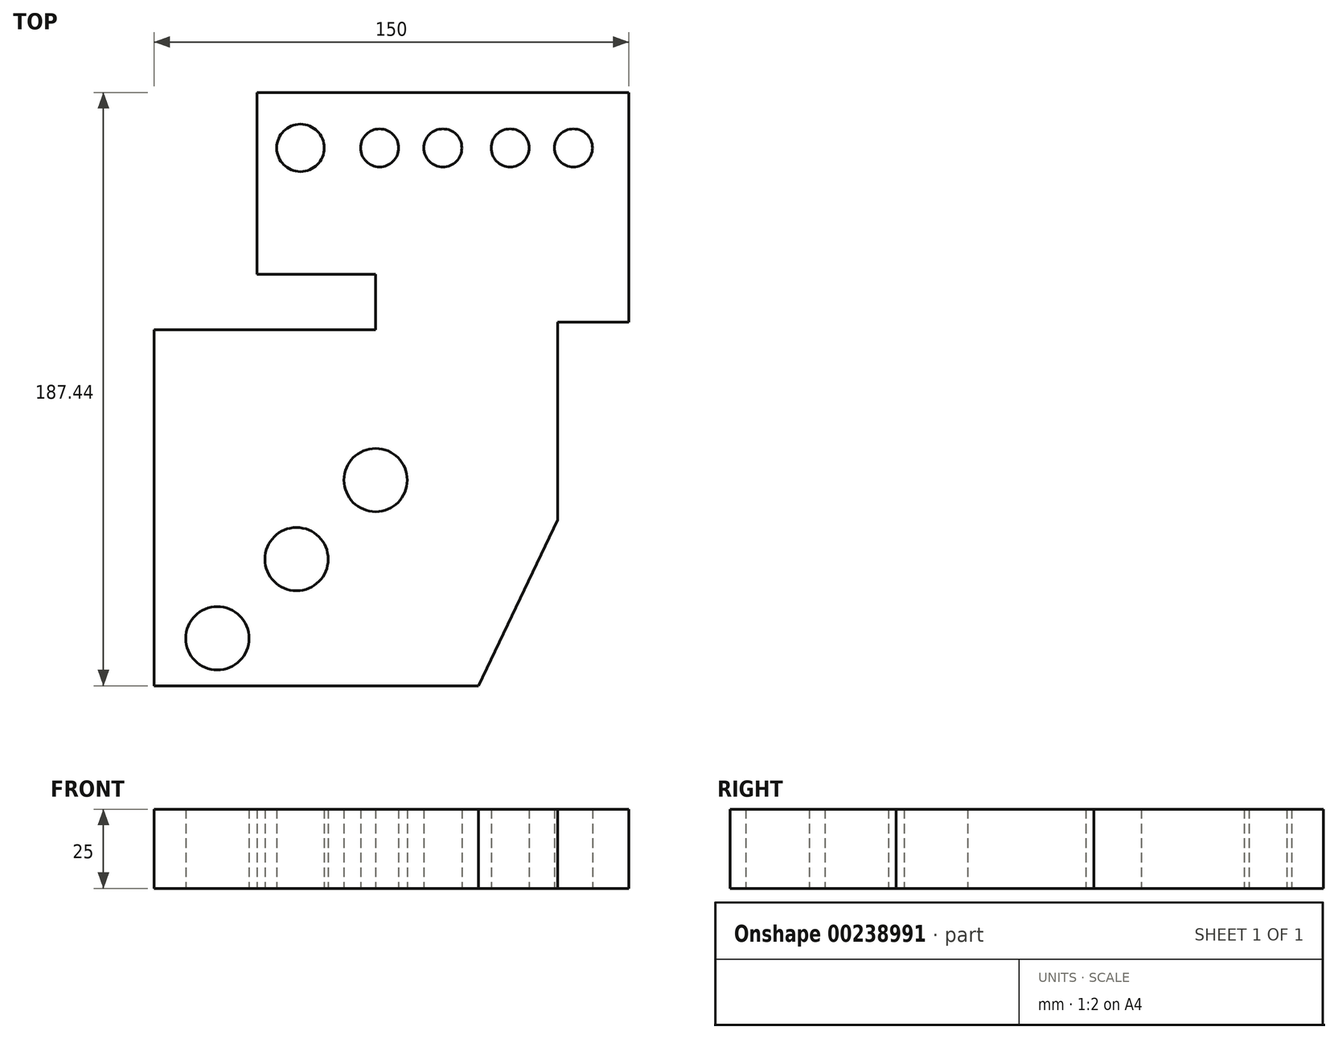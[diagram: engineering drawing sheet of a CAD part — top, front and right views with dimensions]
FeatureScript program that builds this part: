
annotation { "Feature Type Name" : "Feature", "Feature Type Description" : "" }
export const myFeature = defineFeature(function(context is Context, id is Id, definition is map)
    precondition{}
    {
        {
            var Q0;
            Q0=qCreatedBy(makeId("Top.planeOp"),FACE);
            var sketch = newSketch(context, id + "F0", { "sketchPlane" : qUnion([Q0])});
            skLineSegment(sketch, "E0", {"start": v(-120.25, -66.32) * mm, "end": v(-17.75, -66.32) * mm});
            skLineSegment(sketch, "E1", {"start": v(-120.25, -66.32) * mm, "end": v(-120.25, 46.12) * mm});
            skLineSegment(sketch, "E2", {"start": v(-120.25, 46.12) * mm, "end": v(-50.25, 46.12) * mm});
            skLineSegment(sketch, "E3", {"start": v(-50.25, 46.12) * mm, "end": v(-50.25, 63.62) * mm});
            skLineSegment(sketch, "E4", {"start": v(-50.25, 63.62) * mm, "end": v(-87.75, 63.62) * mm});
            skLineSegment(sketch, "E5", {"start": v(-87.75, 63.62) * mm, "end": v(-87.75, 121.12) * mm});
            skLineSegment(sketch, "E6", {"start": v(-87.75, 121.12) * mm, "end": v(29.75, 121.12) * mm});
            skLineSegment(sketch, "E7", {"start": v(29.75, 121.12) * mm, "end": v(29.75, 48.62) * mm});
            skLineSegment(sketch, "E8", {"start": v(29.75, 48.62) * mm, "end": v(7.25, 48.62) * mm});
            skLineSegment(sketch, "E9", {"start": v(7.25, 48.62) * mm, "end": v(7.25, -13.88) * mm});
            skLineSegment(sketch, "E10", {"start": v(7.25, -13.88) * mm, "end": v(-17.75, -66.32) * mm});
            skLineSegment(sketch, "E11", {"start": v(-120.25, -66.32) * mm, "end": v(-100.25, -66.32) * mm});
            skLineSegment(sketch, "E12", {"start": v(-120.25, -66.32) * mm, "end": v(-120.25, -51.32) * mm});
            skLineSegment(sketch, "E13", {"start": v(-120.25, -51.32) * mm, "end": v(-100.25, -51.32) * mm});
            skCircle(sketch, "E14", {"center": v(-100.25, -51.32) * mm, "radius": 10 * mm});
            skLineSegment(sketch, "E15", {"start": v(-100.25, -66.32) * mm, "end": v(-75.25, -66.32) * mm});
            skLineSegment(sketch, "E16", {"start": v(-120.25, -51.32) * mm, "end": v(-120.25, -26.32) * mm});
            skLineSegment(sketch, "E17", {"start": v(-120.25, -26.32) * mm, "end": v(-75.25, -26.32) * mm});
            skCircle(sketch, "E18", {"center": v(-75.25, -26.32) * mm, "radius": 10 * mm});
            skLineSegment(sketch, "E19", {"start": v(-120.25, -26.32) * mm, "end": v(-120.25, -1.32) * mm});
            skLineSegment(sketch, "E20", {"start": v(-75.25, -66.32) * mm, "end": v(-50.25, -66.32) * mm});
            skLineSegment(sketch, "E21", {"start": v(-120.25, -1.32) * mm, "end": v(-50.25, -1.32) * mm});
            skCircle(sketch, "E22", {"center": v(-50.25, -1.32) * mm, "radius": 10 * mm});
            skLineSegment(sketch, "E23", {"start": v(29.75, 121.12) * mm, "end": v(29.75, 103.62) * mm});
            skLineSegment(sketch, "E24", {"start": v(29.75, 121.12) * mm, "end": v(12.25, 121.12) * mm});
            skLineSegment(sketch, "E25", {"start": v(12.25, 121.12) * mm, "end": v(12.25, 103.62) * mm});
            skCircle(sketch, "E26", {"center": v(12.25, 103.62) * mm, "radius": 6 * mm});
            skLineSegment(sketch, "E27", {"start": v(12.25, 121.12) * mm, "end": v(-7.75, 121.12) * mm});
            skLineSegment(sketch, "E28", {"start": v(-7.75, 121.12) * mm, "end": v(-7.75, 103.62) * mm});
            skCircle(sketch, "E29", {"center": v(-7.75, 103.62) * mm, "radius": 6 * mm});
            skLineSegment(sketch, "E30", {"start": v(-103.8, 126.74) * mm, "end": v(-82.76, 132.44) * mm, "construction": true});
            skLineSegment(sketch, "E31", {"start": v(-7.75, 121.12) * mm, "end": v(-29, 121.12) * mm, "construction": true});
            skLineSegment(sketch, "E32", {"start": v(-29, 121.12) * mm, "end": v(-29, 103.62) * mm});
            skCircle(sketch, "E33", {"center": v(-29, 103.62) * mm, "radius": 6 * mm});
            skLineSegment(sketch, "E34", {"start": v(-29, 121.12) * mm, "end": v(-49, 121.12) * mm});
            skLineSegment(sketch, "E35", {"start": v(-49, 121.12) * mm, "end": v(-49, 103.62) * mm});
            skCircle(sketch, "E36", {"center": v(-49, 103.62) * mm, "radius": 6 * mm});
            skLineSegment(sketch, "E37", {"start": v(-49, 121.12) * mm, "end": v(-74, 121.12) * mm});
            skLineSegment(sketch, "E38", {"start": v(-74, 121.12) * mm, "end": v(-74, 103.62) * mm});
            skCircle(sketch, "E39", {"center": v(-74, 103.62) * mm, "radius": 7.5 * mm});
            skSolve(sketch);
        }
        {
            var Q0;
            Q0 = qSketchRegion(id + "F0", true);
            extrude(context, id + "F1", {"entities" : qUnion([Q0]), "depth" : 25 * mm});
        }
    });
